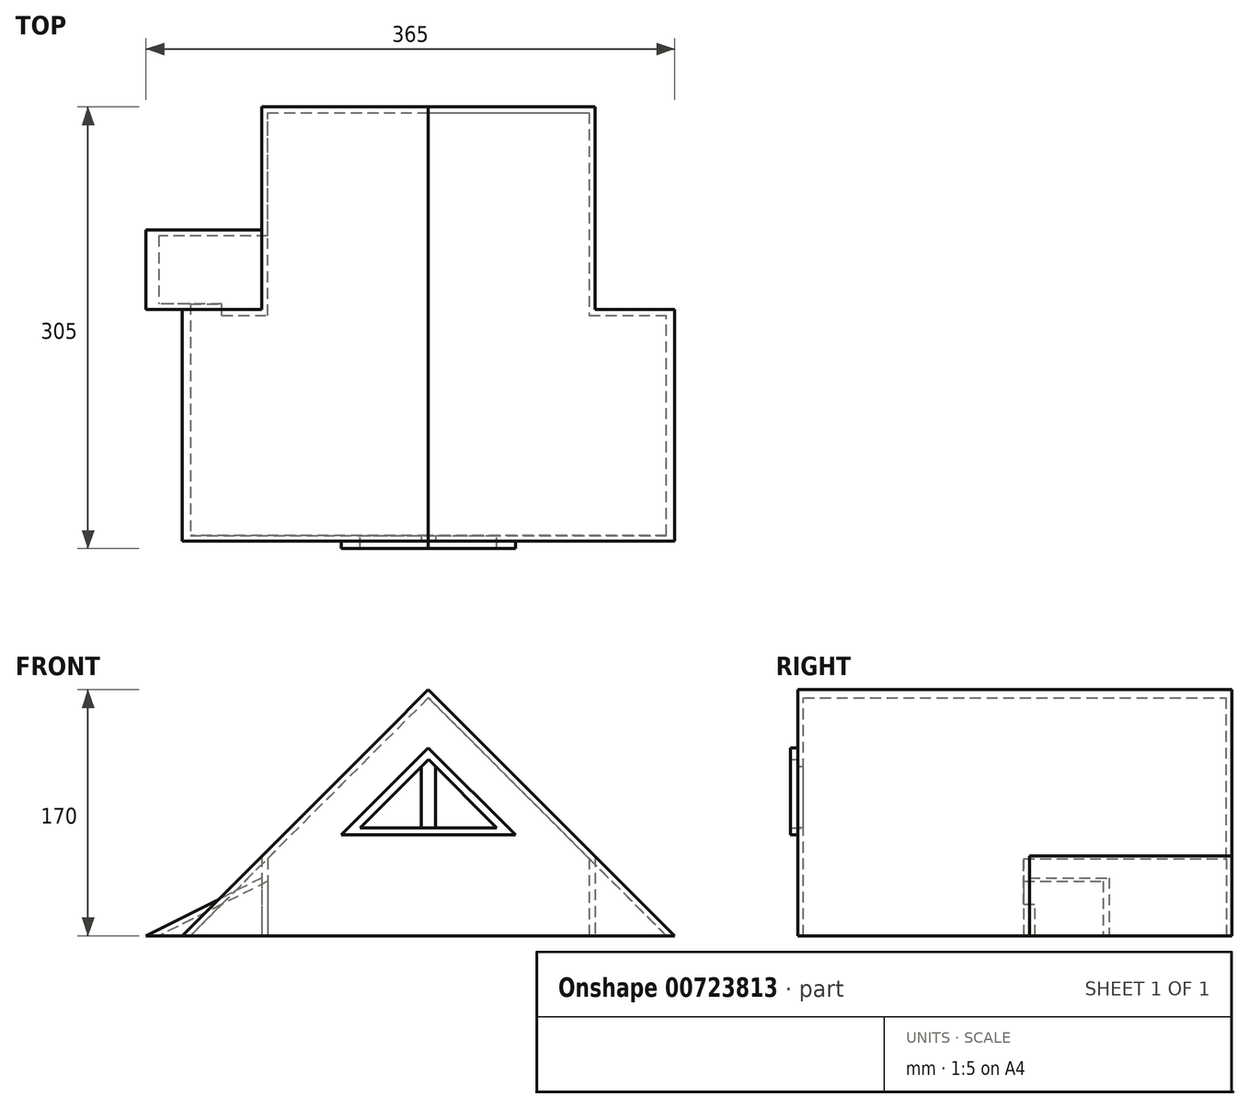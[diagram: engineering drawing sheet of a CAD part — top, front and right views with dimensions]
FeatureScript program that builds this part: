
annotation { "Feature Type Name" : "Feature", "Feature Type Description" : "" }
export const myFeature = defineFeature(function(context is Context, id is Id, definition is map)
    precondition{}
    {
        {
            var Q0;
            Q0=qCreatedBy(makeId("Top.planeOp"),FACE);
            var sketch = newSketch(context, id + "F0", { "sketchPlane" : qUnion([Q0])});
            skLineSegment(sketch, "E0", {"start": v(-185.52, -53.64) * mm, "end": v(154.48, -53.64) * mm});
            skLineSegment(sketch, "E1", {"start": v(154.48, -53.64) * mm, "end": v(154.48, 106.36) * mm});
            skLineSegment(sketch, "E2", {"start": v(154.48, 106.36) * mm, "end": v(99.48, 106.36) * mm});
            skLineSegment(sketch, "E3", {"start": v(-150.52, 106.36) * mm, "end": v(-185.52, 106.36) * mm});
            skLineSegment(sketch, "E4", {"start": v(-185.52, 106.36) * mm, "end": v(-185.52, -53.64) * mm});
            skLineSegment(sketch, "E5", {"start": v(-150.52, 106.36) * mm, "end": v(-60.52, 106.36) * mm});
            skLineSegment(sketch, "E6", {"start": v(99.48, 106.36) * mm, "end": v(-60.52, 106.36) * mm});
            skLineSegment(sketch, "E7", {"start": v(99.48, 246.36) * mm, "end": v(99.48, 106.36) * mm});
            skPoint(sketch, "E8", {"position": v(-130.52, 106.36) * mm});
            skLineSegment(sketch, "E9", {"start": v(-130.52, 106.36) * mm, "end": v(-130.52, 246.36) * mm});
            skLineSegment(sketch, "E10", {"start": v(-130.52, 246.36) * mm, "end": v(99.48, 246.36) * mm});
            skLineSegment(sketch, "E11", {"start": v(-130.52, 161.36) * mm, "end": v(-210.52, 161.36) * mm});
            skLineSegment(sketch, "E12", {"start": v(-210.52, 161.36) * mm, "end": v(-210.52, 106.36) * mm});
            skLineSegment(sketch, "E13", {"start": v(-210.52, 106.36) * mm, "end": v(-185.52, 106.36) * mm});
            skSolve(sketch);
        }
        {
            var Q0;
            Q0=makeQuery(id+"F0.imprint","IMPRINT",FACE,{"disambiguationData":[TD([[makeQuery(id+"F0.imprint","IMPRINT",EDGE,{"derivedFrom":sQuery(id+"F0.wireOp",EDGE,"E0")}),1.0]])]});
            extrude(context, id + "F1", {"entities" : qUnion([Q0]), "depth" : 140 * mm, "offsetDistance" : 25 * mm});
        }
        {
            var Q0;
            Q0=makeQuery(id+"F1.opExtrude","CAP_EDGE",EDGE,{"disambiguationData":[OSD([sQuery(id+"F0.wireOp",EDGE,"E4")])],"isStart":false});
            var Q1;
            Q1=makeQuery(id+"F1.opExtrude","CAP_EDGE",EDGE,{"disambiguationData":[OSD([sQuery(id+"F0.wireOp",EDGE,"E1")])],"isStart":false});
            chamfer(context, id + "F2", {"entities" : qUnion([Q0, Q1]), "width" : 140 * mm, "tangentPropagation" : true});
        }
        {
            var Q0;
            Q0=makeQuery(id+"F1.opExtrude","CAP_FACE",FACE,{"disambiguationData":[OSD([sQuery(id+"F0.wireOp",EDGE,"E0"),sQuery(id+"F0.wireOp",EDGE,"E1"),sQuery(id+"F0.wireOp",EDGE,"E2"),sQuery(id+"F0.wireOp",EDGE,"E3"),sQuery(id+"F0.wireOp",EDGE,"E4"),sQuery(id+"F0.wireOp",EDGE,"E5"),sQuery(id+"F0.wireOp",EDGE,"E6")])],"isStart":false});
            extrude(context, id + "F3", {"entities" : qUnion([Q0]), "operationType" : NewBodyOperationType.ADD, "depth" : 30 * mm, "offsetDistance" : 25 * mm});
        }
        {
            var Q0;
            {var subQ0=sQuery(id+"F0.wireOp",EDGE,"E6");var subQ1=sQuery(id+"F0.wireOp",EDGE,"E5");var subQ2=sQuery(id+"F0.wireOp",EDGE,"E4");var subQ3=sQuery(id+"F0.wireOp",EDGE,"E3");var subQ4=sQuery(id+"F0.wireOp",EDGE,"E2");var subQ5=sQuery(id+"F0.wireOp",EDGE,"E1");var subQ6=sQuery(id+"F0.wireOp",EDGE,"E0");Q0=makeQuery(id+"F3.opExtrude","CAP_EDGE",EDGE,{"disambiguationData":[OSD([subQ6,subQ5,subQ4,subQ3,subQ2,subQ1,subQ0]),TDD([makeQuery(id+"F2.opChamfer","BLEND_EDGE",EDGE,{"blendedFrom":[makeQuery(id+"F1.opExtrude","CAP_EDGE",EDGE,{"disambiguationData":[OSD([subQ2])],"isStart":false}),makeQuery(id+"F1.opExtrude","CAP_FACE",FACE,{"disambiguationData":[OSD([subQ6,subQ5,subQ4,subQ3,subQ2,subQ1,subQ0])],"isStart":false})],"blendedInto":[makeQuery(id+"F1.opExtrude","CAP_FACE",FACE,{"disambiguationData":[OSD([subQ6,subQ5,subQ4,subQ3,subQ2,subQ1,subQ0])],"isStart":false})]})])],"isStart":false});}
            var Q1;
            {var subQ0=sQuery(id+"F0.wireOp",EDGE,"E6");var subQ1=sQuery(id+"F0.wireOp",EDGE,"E5");var subQ2=sQuery(id+"F0.wireOp",EDGE,"E4");var subQ3=sQuery(id+"F0.wireOp",EDGE,"E3");var subQ4=sQuery(id+"F0.wireOp",EDGE,"E2");var subQ5=sQuery(id+"F0.wireOp",EDGE,"E1");var subQ6=sQuery(id+"F0.wireOp",EDGE,"E0");Q1=makeQuery(id+"F3.opExtrude","CAP_EDGE",EDGE,{"disambiguationData":[OSD([subQ6,subQ5,subQ4,subQ3,subQ2,subQ1,subQ0]),TDD([makeQuery(id+"F2.opChamfer","BLEND_EDGE",EDGE,{"blendedFrom":[makeQuery(id+"F1.opExtrude","CAP_EDGE",EDGE,{"disambiguationData":[OSD([subQ5])],"isStart":false}),makeQuery(id+"F1.opExtrude","CAP_FACE",FACE,{"disambiguationData":[OSD([subQ6,subQ5,subQ4,subQ3,subQ2,subQ1,subQ0])],"isStart":false})],"blendedInto":[makeQuery(id+"F1.opExtrude","CAP_FACE",FACE,{"disambiguationData":[OSD([subQ6,subQ5,subQ4,subQ3,subQ2,subQ1,subQ0])],"isStart":false})]})])],"isStart":false});}
            chamfer(context, id + "F4", {"entities" : qUnion([Q0, Q1]), "width" : 30 * mm, "tangentPropagation" : true});
        }
        {
            var Q0;
            {var subQ1=sQuery(id+"F0.wireOp",EDGE,"E6");Q0=makeQuery(id+"F0.imprint","IMPRINT",FACE,{"disambiguationData":[TD([[makeQuery(id+"F0.imprint","IMPRINT",EDGE,{"derivedFrom":subQ1}),-1.0]])]});}
            extrude(context, id + "F5", {"entities" : qUnion([Q0]), "operationType" : NewBodyOperationType.ADD, "depth" : 140 * mm, "offsetDistance" : 25 * mm});
        }
        {
            var Q0;
            Q0=makeQuery(id+"F5.opExtrude","CAP_EDGE",EDGE,{"disambiguationData":[OSD([sQuery(id+"F0.wireOp",EDGE,"E9")])],"isStart":false});
            chamfer(context, id + "F6", {"entities" : qUnion([Q0]), "width" : 85 * mm, "tangentPropagation" : true});
        }
        {
            var Q0;
            Q0=makeQuery(id+"F5.opExtrude","CAP_EDGE",EDGE,{"disambiguationData":[OSD([sQuery(id+"F0.wireOp",EDGE,"E7")])],"isStart":false});
            chamfer(context, id + "F7", {"entities" : qUnion([Q0]), "width" : 85 * mm, "tangentPropagation" : true});
        }
        {
            var Q0;
            Q0=makeQuery(id+"F5.opExtrude","CAP_FACE",FACE,{"disambiguationData":[OSD([sQuery(id+"F0.wireOp",EDGE,"E5"),sQuery(id+"F0.wireOp",EDGE,"E6"),sQuery(id+"F0.wireOp",EDGE,"E7"),sQuery(id+"F0.wireOp",EDGE,"E9"),sQuery(id+"F0.wireOp",EDGE,"E10")])],"isStart":false});
            extrude(context, id + "F8", {"entities" : qUnion([Q0]), "operationType" : NewBodyOperationType.ADD, "depth" : 30 * mm, "offsetDistance" : 25 * mm});
        }
        {
            var Q0;
            {var subQ0=sQuery(id+"F0.wireOp",EDGE,"E10");var subQ1=sQuery(id+"F0.wireOp",EDGE,"E9");var subQ2=sQuery(id+"F0.wireOp",EDGE,"E7");var subQ3=sQuery(id+"F0.wireOp",EDGE,"E6");var subQ4=sQuery(id+"F0.wireOp",EDGE,"E5");Q0=makeQuery(id+"F8.opExtrude","CAP_EDGE",EDGE,{"disambiguationData":[OSD([subQ4,subQ3,subQ2,subQ1,subQ0]),TDD([makeQuery(id+"F6.opChamfer","BLEND_EDGE",EDGE,{"blendedFrom":[makeQuery(id+"F5.opExtrude","CAP_EDGE",EDGE,{"disambiguationData":[OSD([subQ1])],"isStart":false}),makeQuery(id+"F5.opExtrude","CAP_FACE",FACE,{"disambiguationData":[OSD([subQ4,subQ3,subQ2,subQ1,subQ0])],"isStart":false})],"blendedInto":[makeQuery(id+"F5.opExtrude","CAP_FACE",FACE,{"disambiguationData":[OSD([subQ4,subQ3,subQ2,subQ1,subQ0])],"isStart":false})]})])],"isStart":false});}
            var Q1;
            {var subQ0=sQuery(id+"F0.wireOp",EDGE,"E10");var subQ1=sQuery(id+"F0.wireOp",EDGE,"E9");var subQ2=sQuery(id+"F0.wireOp",EDGE,"E7");var subQ3=sQuery(id+"F0.wireOp",EDGE,"E6");var subQ4=sQuery(id+"F0.wireOp",EDGE,"E5");Q1=makeQuery(id+"F8.opExtrude","CAP_EDGE",EDGE,{"disambiguationData":[OSD([subQ4,subQ3,subQ2,subQ1,subQ0]),TDD([makeQuery(id+"F7.opChamfer","BLEND_EDGE",EDGE,{"blendedFrom":[makeQuery(id+"F5.opExtrude","CAP_EDGE",EDGE,{"disambiguationData":[OSD([subQ2])],"isStart":false}),makeQuery(id+"F5.opExtrude","CAP_FACE",FACE,{"disambiguationData":[OSD([subQ4,subQ3,subQ2,subQ1,subQ0])],"isStart":false})],"blendedInto":[makeQuery(id+"F5.opExtrude","CAP_FACE",FACE,{"disambiguationData":[OSD([subQ4,subQ3,subQ2,subQ1,subQ0])],"isStart":false})]})])],"isStart":false});}
            chamfer(context, id + "F9", {"entities" : qUnion([Q0, Q1]), "width" : 30 * mm, "tangentPropagation" : true});
        }
        {
            var Q0;
            {var subQ4=sQuery(id+"F0.wireOp",EDGE,"E3");Q0=makeQuery(id+"F0.imprint","IMPRINT",FACE,{"disambiguationData":[TD([[makeQuery(id+"F0.imprint","IMPRINT",EDGE,{"derivedFrom":subQ4}),-1.0]])]});}
            extrude(context, id + "F10", {"entities" : qUnion([Q0]), "operationType" : NewBodyOperationType.ADD, "depth" : 40 * mm, "offsetDistance" : 25 * mm});
        }
        {
            var Q0;
            Q0=makeQuery(id+"F10.opExtrude","SWEPT_FACE",FACE,{"disambiguationData":[OSD([sQuery(id+"F0.wireOp",EDGE,"E11")])]});
            var sketch = newSketch(context, id + "F11", { "sketchPlane" : qUnion([Q0])});
            skLineSegment(sketch, "E14.0.0", {"start": v(130.52, 0) * mm, "end": v(210.52, 0) * mm});
            skLineSegment(sketch, "E14.0.1", {"start": v(210.52, 0) * mm, "end": v(210.52, 40) * mm});
            skLineSegment(sketch, "E14.0.2", {"start": v(210.52, 40) * mm, "end": v(130.52, 40) * mm});
            skLineSegment(sketch, "E14.0.3", {"start": v(130.52, 40) * mm, "end": v(130.52, 0) * mm});
            skLineSegment(sketch, "E15", {"start": v(130.52, 40) * mm, "end": v(210.52, 0) * mm});
            skSolve(sketch);
        }
        {
            var Q0;
            Q0=makeQuery(id+"F11.imprint","IMPRINT",FACE,{"disambiguationData":[TD([[makeQuery(id+"F11.imprint","IMPRINT",EDGE,{"derivedFrom":sQuery(id+"F11.wireOp",EDGE,"E14.0.1")}),-1.0]])]});
            extrude(context, id + "F12", {"entities" : qUnion([Q0]), "operationType" : NewBodyOperationType.REMOVE, "oppositeDirection" : true, "depth" : 55 * mm, "offsetDistance" : 25 * mm});
        }
        {
            var Q0;
            {var subQ0=sQuery(id+"F0.wireOp",EDGE,"E0");Q0=makeQuery(id+"F3.boolean.opBoolean","MERGE",FACE,{"derivedFrom":[makeQuery(id+"F1.opExtrude","SWEPT_FACE",FACE,{"disambiguationData":[OSD([subQ0])]}),makeQuery(id+"F3.opExtrude","SWEPT_FACE",FACE,{"disambiguationData":[OSD([subQ0])]})]});}
            var sketch = newSketch(context, id + "F13", { "sketchPlane" : qUnion([Q0])});
            skLineSegment(sketch, "E16", {"start": v(-15.52, 129.74) * mm, "end": v(-75.62, 69.64) * mm});
            skLineSegment(sketch, "E17", {"start": v(-15.52, 129.74) * mm, "end": v(44.59, 69.64) * mm});
            skLineSegment(sketch, "E18", {"start": v(44.59, 69.64) * mm, "end": v(-75.62, 69.64) * mm});
            skPoint(sketch, "E19", {"position": v(-15.42, 121.74) * mm});
            skLineSegment(sketch, "E20", {"start": v(-15.42, 121.74) * mm, "end": v(-62.53, 74.64) * mm});
            skLineSegment(sketch, "E21", {"start": v(-15.42, 121.74) * mm, "end": v(31.68, 74.64) * mm});
            skLineSegment(sketch, "E22", {"start": v(31.68, 74.64) * mm, "end": v(-62.53, 74.64) * mm});
            skLineSegment(sketch, "E23", {"start": v(-15.42, 121.74) * mm, "end": v(-15.42, 74.64) * mm});
            skLineSegment(sketch, "E24", {"start": v(-15.42, 74.64) * mm, "end": v(-20.42, 74.64) * mm});
            skLineSegment(sketch, "E25", {"start": v(-20.42, 74.64) * mm, "end": v(-20.42, 116.74) * mm});
            skLineSegment(sketch, "E26", {"start": v(-15.42, 74.64) * mm, "end": v(-10.42, 74.64) * mm});
            skLineSegment(sketch, "E27", {"start": v(-10.42, 74.64) * mm, "end": v(-10.42, 116.74) * mm});
            skSolve(sketch);
        }
        {
            var Q0;
            Q0=makeQuery(id+"F13.imprint","IMPRINT",FACE,{"disambiguationData":[TD([[makeQuery(id+"F13.imprint","IMPRINT",EDGE,{"derivedFrom":sQuery(id+"F13.wireOp",EDGE,"E16")}),1.0]])]});
            extrude(context, id + "F14", {"entities" : qUnion([Q0]), "operationType" : NewBodyOperationType.ADD, "depth" : 5 * mm, "offsetDistance" : 25 * mm});
        }
        {
            var Q0;
            {var subQ0=sQuery(id+"F0.wireOp",EDGE,"E9");var subQ1=sQuery(id+"F0.wireOp",EDGE,"E5");var subQ2=sQuery(id+"F0.wireOp",EDGE,"E3");var subQ3=sQuery(id+"F0.wireOp",EDGE,"E6");Q0=makeQuery(id+"F10.boolean.opBoolean","MERGE",FACE,{"derivedFrom":[makeQuery(id+"F5.boolean.opBoolean","MERGE",FACE,{"derivedFrom":[makeQuery(id+"F1.opExtrude","CAP_FACE",FACE,{"disambiguationData":[OSD([sQuery(id+"F0.wireOp",EDGE,"E0"),sQuery(id+"F0.wireOp",EDGE,"E1"),sQuery(id+"F0.wireOp",EDGE,"E2"),subQ2,sQuery(id+"F0.wireOp",EDGE,"E4"),subQ1,subQ3])],"isStart":true}),makeQuery(id+"F5.opExtrude","CAP_FACE",FACE,{"disambiguationData":[OSD([subQ1,subQ3,sQuery(id+"F0.wireOp",EDGE,"E7"),subQ0,sQuery(id+"F0.wireOp",EDGE,"E10")])],"isStart":true})]}),makeQuery(id+"F10.opExtrude","CAP_FACE",FACE,{"disambiguationData":[OSD([subQ2,subQ1,subQ0,sQuery(id+"F0.wireOp",EDGE,"E11"),sQuery(id+"F0.wireOp",EDGE,"E12"),sQuery(id+"F0.wireOp",EDGE,"E13")])],"isStart":true})]});}
            shell(context, id + "F15", {"entities" : qUnion([Q0]), "thickness" : 4 * mm});
        }
        {
            var Q0;
            {var subQ3=sQuery(id+"F13.wireOp",EDGE,"E25");Q0=makeQuery(id+"F13.imprint","IMPRINT",FACE,{"disambiguationData":[TD([[makeQuery(id+"F13.imprint","IMPRINT",EDGE,{"derivedFrom":subQ3}),1.0]])]});}
            var Q1;
            {var subQ3=sQuery(id+"F13.wireOp",EDGE,"E27");Q1=makeQuery(id+"F13.imprint","IMPRINT",FACE,{"disambiguationData":[TD([[makeQuery(id+"F13.imprint","IMPRINT",EDGE,{"derivedFrom":subQ3}),-1.0]])]});}
            extrude(context, id + "F16", {"entities" : qUnion([Q0, Q1]), "operationType" : NewBodyOperationType.REMOVE, "oppositeDirection" : true, "depth" : 25 * mm, "offsetDistance" : 25 * mm});
        }
    });
